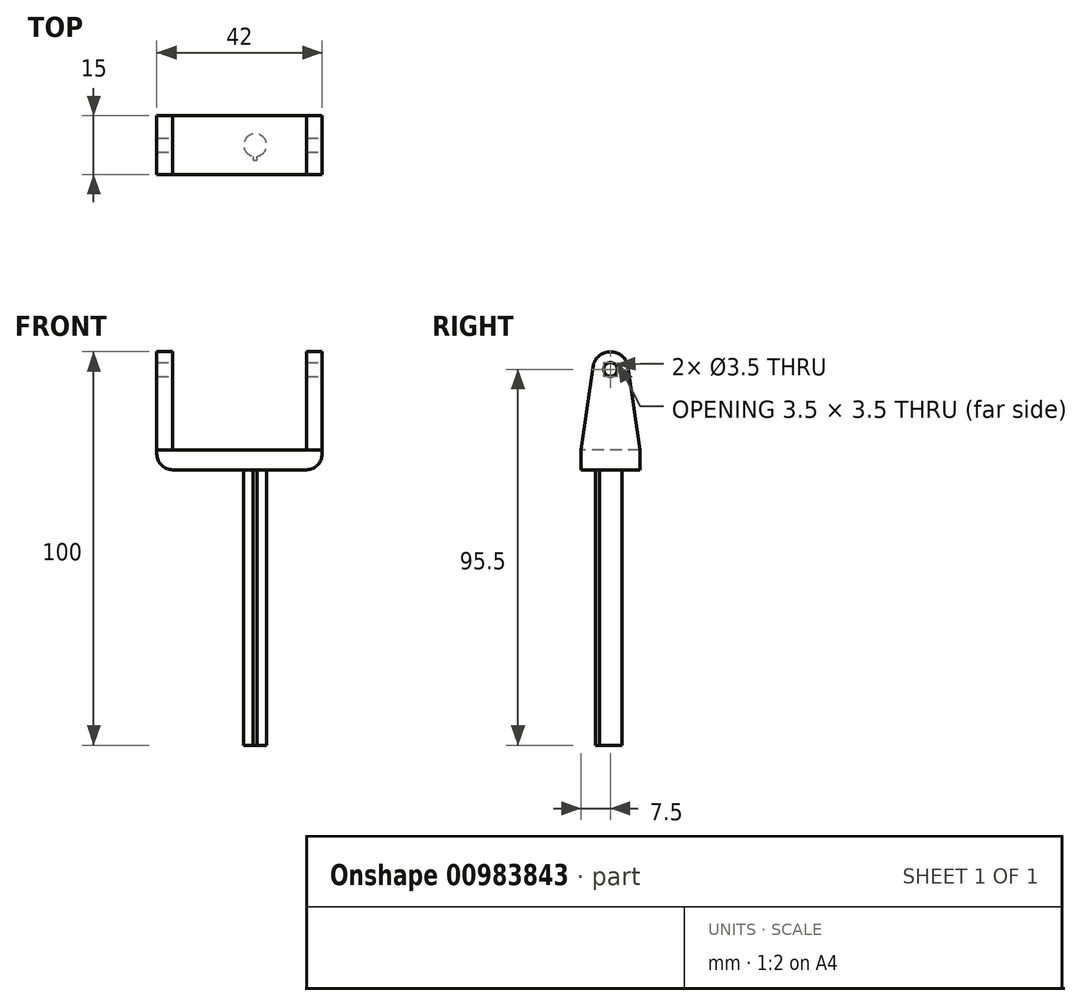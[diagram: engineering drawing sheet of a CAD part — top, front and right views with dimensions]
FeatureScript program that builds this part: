
annotation { "Feature Type Name" : "Feature", "Feature Type Description" : "" }
export const myFeature = defineFeature(function(context is Context, id is Id, definition is map)
    precondition{}
    {
        {
            var Q0;
            Q0=qCreatedBy(makeId("Top.planeOp"),FACE);
            var sketch = newSketch(context, id + "F0", { "sketchPlane" : qUnion([Q0])});
            skCircle(sketch, "E0", {"center": v(0, 0) * mm, "radius": 2.9 * mm});
            skSolve(sketch);
        }
        {
            var Q0;
            Q0=makeQuery(id+"F0.imprint","IMPRINT",FACE,{"disambiguationData":[TD([[makeQuery(id+"F0.imprint","IMPRINT",EDGE,{"derivedFrom":sQuery(id+"F0.wireOp",EDGE,"E0")}),1.0]])]});
            extrude(context, id + "F1", {"entities" : qUnion([Q0]), "depth" : 70 * mm, "offsetDistance" : 25 * mm});
        }
        {
            var Q0;
            Q0=makeQuery(id+"F1.opExtrude","CAP_FACE",FACE,{"disambiguationData":[OSD([sQuery(id+"F0.wireOp",EDGE,"E0")])],"isStart":false});
            var sketch = newSketch(context, id + "F2", { "sketchPlane" : qUnion([Q0])});
            skLineSegment(sketch, "E1.bottom", {"start": v(17, -7.5) * mm, "end": v(-25, -7.5) * mm});
            skLineSegment(sketch, "E1.top", {"start": v(17, 7.5) * mm, "end": v(-25, 7.5) * mm});
            skLineSegment(sketch, "E1.left", {"start": v(17, -7.5) * mm, "end": v(17, 7.5) * mm});
            skLineSegment(sketch, "E1.right", {"start": v(-25, -7.5) * mm, "end": v(-25, 7.5) * mm});
            skSolve(sketch);
        }
        {
            var Q0;
            Q0 = qSketchRegion(id + "F2", true);
            extrude(context, id + "F3", {"entities" : qUnion([Q0]), "operationType" : NewBodyOperationType.ADD, "depth" : 5 * mm, "offsetDistance" : 25 * mm});
        }
        {
            var Q0;
            Q0=makeQuery(id+"F3.opExtrude","CAP_FACE",FACE,{"disambiguationData":[OSD([sQuery(id+"F2.wireOp",EDGE,"E1.bottom"),sQuery(id+"F2.wireOp",EDGE,"E1.top"),sQuery(id+"F2.wireOp",EDGE,"E1.left"),sQuery(id+"F2.wireOp",EDGE,"E1.right")])],"isStart":false});
            var sketch = newSketch(context, id + "F4", { "sketchPlane" : qUnion([Q0])});
            skLineSegment(sketch, "E2.bottom", {"start": v(-25, 7.5) * mm, "end": v(-21, 7.5) * mm});
            skLineSegment(sketch, "E2.top", {"start": v(-25, -7.5) * mm, "end": v(-21, -7.5) * mm});
            skLineSegment(sketch, "E2.left", {"start": v(-25, 7.5) * mm, "end": v(-25, -7.5) * mm});
            skLineSegment(sketch, "E2.right", {"start": v(-21, 7.5) * mm, "end": v(-21, -7.5) * mm});
            skLineSegment(sketch, "E3.bottom", {"start": v(17, -7.5) * mm, "end": v(13, -7.5) * mm});
            skLineSegment(sketch, "E3.top", {"start": v(17, 7.5) * mm, "end": v(13, 7.5) * mm});
            skLineSegment(sketch, "E3.left", {"start": v(17, -7.5) * mm, "end": v(17, 7.5) * mm});
            skLineSegment(sketch, "E3.right", {"start": v(13, -7.5) * mm, "end": v(13, 7.5) * mm});
            skSolve(sketch);
        }
        {
            var Q0;
            Q0=makeQuery(id+"F4.imprint","IMPRINT",FACE,{"disambiguationData":[TD([[makeQuery(id+"F4.imprint","IMPRINT",EDGE,{"derivedFrom":sQuery(id+"F4.wireOp",EDGE,"E2.bottom")}),1.0]])]});
            var Q1;
            Q1=makeQuery(id+"F4.imprint","IMPRINT",FACE,{"disambiguationData":[TD([[makeQuery(id+"F4.imprint","IMPRINT",EDGE,{"derivedFrom":sQuery(id+"F4.wireOp",EDGE,"E3.bottom")}),-1.0]])]});
            extrude(context, id + "F5", {"entities" : qUnion([Q0, Q1]), "operationType" : NewBodyOperationType.ADD, "depth" : 25 * mm, "offsetDistance" : 25 * mm});
        }
        {
            var Q0;
            Q0=makeQuery(id+"F5.boolean.opBoolean","MERGE",FACE,{"derivedFrom":[makeQuery(id+"F3.opExtrude","SWEPT_FACE",FACE,{"disambiguationData":[OSD([sQuery(id+"F2.wireOp",EDGE,"E1.left")])]}),makeQuery(id+"F5.opExtrude","SWEPT_FACE",FACE,{"disambiguationData":[OSD([sQuery(id+"F4.wireOp",EDGE,"E3.left")])]})]});
            var sketch = newSketch(context, id + "F6", { "sketchPlane" : qUnion([Q0])});
            skCircle(sketch, "E4", {"center": v(0, 95.5) * mm, "radius": 1.75 * mm});
            skPoint(sketch, "E4.centerSnap0", {"position": v(0, 100) * mm});
            skArc(sketch, "E5", {"start": v(-4.45, 96.14) * mm, "mid": v(0, 100) * mm, "end": v(4.45, 96.14) * mm});
            skLineSegment(sketch, "E6", {"start": v(-4.45, 96.14) * mm, "end": v(-7.5, 75) * mm});
            skLineSegment(sketch, "E7", {"start": v(4.45, 96.14) * mm, "end": v(7.5, 75) * mm});
            skSolve(sketch);
        }
        {
            var Q0;
            {var subQ0=sQuery(id+"F6.wireOp",EDGE,"E6");Q0=makeQuery(id+"F6.imprint","IMPRINT",FACE,{"disambiguationData":[TD([[makeQuery(id+"F6.imprint","IMPRINT",EDGE,{"derivedFrom":subQ0}),-1.0]])]});}
            var Q1;
            Q1=makeQuery(id+"F6.imprint","IMPRINT",FACE,{"disambiguationData":[TD([[makeQuery(id+"F6.imprint","IMPRINT",EDGE,{"derivedFrom":sQuery(id+"F6.wireOp",EDGE,"E4")}),1.0]])]});
            var Q2;
            {var subQ0=sQuery(id+"F6.wireOp",EDGE,"E7");Q2=makeQuery(id+"F6.imprint","IMPRINT",FACE,{"disambiguationData":[TD([[makeQuery(id+"F6.imprint","IMPRINT",EDGE,{"derivedFrom":subQ0}),1.0]])]});}
            extrude(context, id + "F7", {"entities" : qUnion([Q0, Q1, Q2]), "operationType" : NewBodyOperationType.REMOVE, "oppositeDirection" : true, "depth" : 50 * mm, "offsetDistance" : 25 * mm});
        }
        {
            var Q0;
            Q0=makeQuery(id+"F3.opExtrude","CAP_EDGE",EDGE,{"disambiguationData":[OSD([sQuery(id+"F2.wireOp",EDGE,"E1.right")])],"isStart":true});
            var Q1;
            Q1=makeQuery(id+"F3.opExtrude","CAP_EDGE",EDGE,{"disambiguationData":[OSD([sQuery(id+"F2.wireOp",EDGE,"E1.left")])],"isStart":true});
            fillet(context, id + "F8", {"entities" : qUnion([Q0, Q1]), "radius" : 4 * mm, "tangentPropagation" : true, "allowEdgeOverflow" : false});
        }
        {
            var Q0;
            Q0=makeQuery(id+"F3.opExtrude","CAP_FACE",FACE,{"disambiguationData":[OSD([sQuery(id+"F2.wireOp",EDGE,"E1.bottom"),sQuery(id+"F2.wireOp",EDGE,"E1.top"),sQuery(id+"F2.wireOp",EDGE,"E1.left"),sQuery(id+"F2.wireOp",EDGE,"E1.right")])],"isStart":true});
            var sketch = newSketch(context, id + "F9", { "sketchPlane" : qUnion([Q0])});
            skCircle(sketch, "E8", {"center": v(0, 0) * mm, "radius": 2.9 * mm});
            skLineSegment(sketch, "E9", {"start": v(-0.5, 2.86) * mm, "end": v(-0.5, 3.86) * mm});
            skLineSegment(sketch, "E10", {"start": v(-0.5, 3.86) * mm, "end": v(0.5, 3.86) * mm});
            skLineSegment(sketch, "E11", {"start": v(0.5, 3.86) * mm, "end": v(0.5, 2.86) * mm});
            skPoint(sketch, "E12", {"position": v(0, 2.9) * mm});
            skPoint(sketch, "E13", {"position": v(0, 3.86) * mm});
            skSolve(sketch);
        }
        {
            var Q0;
            Q0 = qSketchRegion(id + "F9", true);
            extrude(context, id + "F10", {"entities" : qUnion([Q0]), "operationType" : NewBodyOperationType.ADD, "depth" : 70 * mm, "offsetDistance" : 25 * mm});
        }
    });
